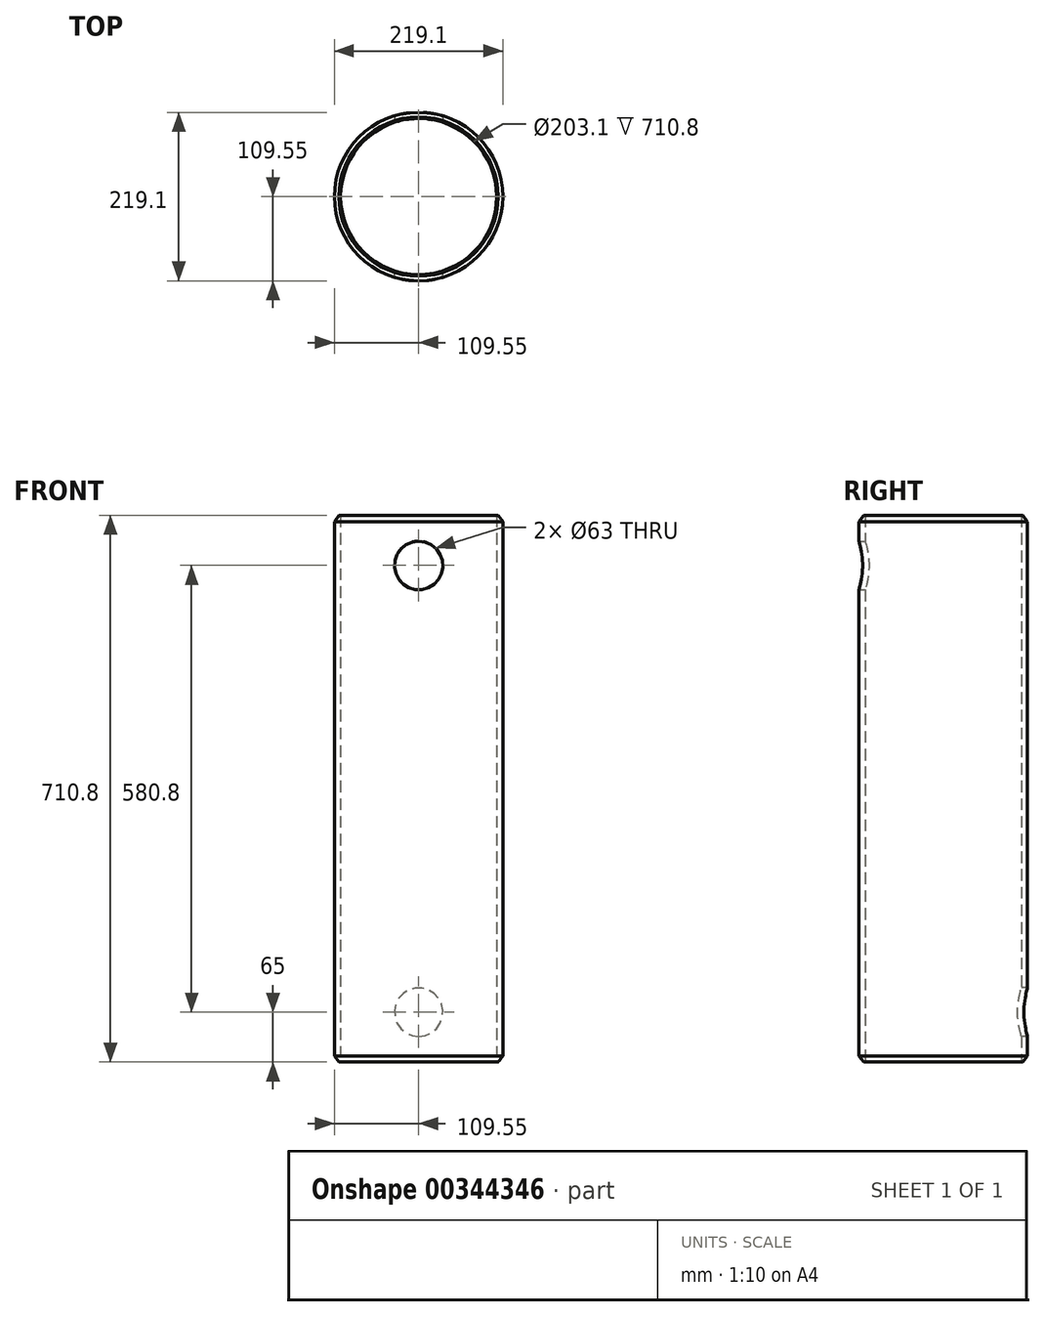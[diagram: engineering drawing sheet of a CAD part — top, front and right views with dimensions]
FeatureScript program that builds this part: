
annotation { "Feature Type Name" : "Feature", "Feature Type Description" : "" }
export const myFeature = defineFeature(function(context is Context, id is Id, definition is map)
    precondition{}
    {
        {
            var Q0;
            Q0=qCreatedBy(makeId("Top.planeOp"),FACE);
            var sketch = newSketch(context, id + "F0", { "sketchPlane" : qUnion([Q0])});
            skCircle(sketch, "E0", {"center": v(0, 0) * mm, "radius": 109.55 * mm});
            skCircle(sketch, "E1.0", {"center": v(0, 0) * mm, "radius": 101.55 * mm});
            skSolve(sketch);
        }
        {
            var Q0;
            Q0=makeQuery(id+"F0.imprint","IMPRINT",FACE,{"disambiguationData":[TD([[makeQuery(id+"F0.imprint","IMPRINT",EDGE,{"derivedFrom":sQuery(id+"F0.wireOp",EDGE,"E0")}),1.0]])]});
            extrude(context, id + "F1", {"entities" : qUnion([Q0]), "depth" : (((450 + 147) - 0.2 + 114)) * mm});
        }
        {
            var Q0;
            Q0=makeQuery(id+"F1.opExtrude","CAP_EDGE",EDGE,{"disambiguationData":[OSD([sQuery(id+"F0.wireOp",EDGE,"E0")])],"isStart":false});
            var Q1;
            Q1=makeQuery(id+"F1.opExtrude","CAP_EDGE",EDGE,{"disambiguationData":[OSD([sQuery(id+"F0.wireOp",EDGE,"E0")])],"isStart":true});
            chamfer(context, id + "F2", {"entities" : qUnion([Q0, Q1]), "chamferType" : ChamferType.OFFSET_ANGLE, "width" : 6 * mm, "oppositeDirection" : false, "angle" : 53 * degree, "tangentPropagation" : true});
        }
        {
            var Q0;
            Q0=qCreatedBy(makeId("Front.planeOp"),FACE);
            var sketch = newSketch(context, id + "F3", { "sketchPlane" : qUnion([Q0])});
            skCircle(sketch, "E2", {"center": v(0, 645.8) * mm, "radius": 31.5 * mm});
            skLineSegment(sketch, "E3", {"start": v(0, 0) * mm, "end": v(0, 956.55) * mm, "construction": true});
            skCircle(sketch, "E4.0.1.0", {"center": v(0, 65) * mm, "radius": 31.5 * mm});
            skLineSegment(sketch, "E4.direction1", {"start": v(0, 645.8) * mm, "end": v(25, 645.8) * mm, "construction": true});
            skLineSegment(sketch, "E4.direction2", {"start": v(0, 645.8) * mm, "end": v(0, 65) * mm, "construction": true});
            skSolve(sketch);
        }
        {
            var Q0;
            Q0=makeQuery(id+"F3.imprint","IMPRINT",FACE,{"disambiguationData":[TD([[makeQuery(id+"F3.imprint","IMPRINT",EDGE,{"derivedFrom":sQuery(id+"F3.wireOp",EDGE,"E2")}),1.0]])]});
            extrude(context, id + "F4", {"entities" : qUnion([Q0]), "operationType" : NewBodyOperationType.REMOVE, "endBound" : BoundingType.THROUGH_ALL, "depth" : 25 * mm});
        }
        {
            var Q0;
            Q0=makeQuery(id+"F3.imprint","IMPRINT",FACE,{"disambiguationData":[TD([[makeQuery(id+"F3.imprint","IMPRINT",EDGE,{"derivedFrom":sQuery(id+"F3.wireOp",EDGE,"E4.0.1.0")}),1.0]])]});
            extrude(context, id + "F5", {"entities" : qUnion([Q0]), "operationType" : NewBodyOperationType.REMOVE, "endBound" : BoundingType.THROUGH_ALL, "oppositeDirection" : true, "depth" : 25 * mm});
        }
    });
